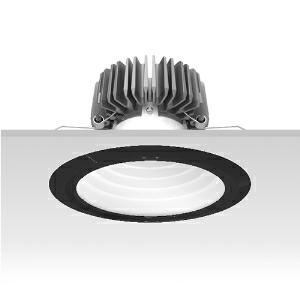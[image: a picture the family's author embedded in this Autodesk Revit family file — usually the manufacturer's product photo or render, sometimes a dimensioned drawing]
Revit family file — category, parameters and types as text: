
# Revit family: 3f_filippi_-_3f_reno_bianco_ampio_3f_filippi_-_30650_a01026_-_3f_reno_200_wh_2000-930_ep_wide___vt_bk_8b70
name_source: partatom
category: Lighting Fixtures
units: mm (PartAtom-declared; Revit-internal decimal feet)

## family parameters
Cut with Voids When Loaded = No
Host = Face
Light Source = No
Part Type = Normal
Room Calculation Point = No
Round Connector Dimension = Use Diameter
Shared = No

## types (1)
- 3F Filippi - 3F Reno Bianco Ampio (1 x LED, 1804 lm, 25 W, 3000 K)
    Apparent Load = 25 VA
    Approval mark = ENEC
    CIE Flux Codes = 75 94 99 100 100
    Color Rendering = 90
    Color Temperature = 3000 K
    Control Gear = Electronic ballast
    Default Elevation = 1800 mm
    Description = ILLUMINOTECHNICAL
Luminous efficiency 100% (DLOR 100%, ULOR 0%).
Initial luminous flux of the luminaire 1804 lm.
Emergency luminaire luminous flux BLF 16.7%.
Direct symmetric wide distribution.
Installation Interdistance Transv.D = 1.56 x hu - Long.D = 1.56 x hu.
Average luminance <3000 cd/m² for radial angles >65°.
Tabular UGR (CIE 117 - 4H-8H; S=0.25H; 70/50/20): RUG 20.6 - 20.5.
Beam angle: 74° - 74°.
Luminous efficacy 72 lm/W.
Lifetime (L90/B10): 30000 h. (tq+25°C)
Lifetime (L85/B10): 50000 h. (tq+25°C)
Lifetime (L70/B10): 80000 h. (tq+25°C)
Sudden decreased luminous flux after 50000 hours: 0% (C0).
Photobiological safety in compliance with IEC/TR 62778: RG0 risk exempt, (IEC 62471).
In compliance with IEC/EN 62722-2-1 - IEC/EN 62717 standards.

SOURCE
Compact LED module 2000/930.
Energy efficiency class (UE 2019/2020 - UE 2019/2015): E.
CIE 13.3 Colour rendering index: CRI >90 (R9 >50%).
IES TM-30 Fidelity Index: Rf = 92 Rg = 101.
CCT nominal colour temperature 3000 K.
Colour initial tolerance (MacAdam): SDCM 3.
Zhaga Book 3 compliant.

MECHANICAL
Passive heat dissipator in die-casting aluminium, oversized, for optimum thermal management of the LED module.
Parabolic element with graduated/concentric rings in white polycarbonate.
Transparent external lens with glossy and satin differentiated surfaces, with a cooling and anti-insect system in methacrylate (PMMA).
Fastening spring clips in stainless steel.
Dimensions: diameter 226 mm, height 146 mm. Weight 1.615 kg.
IP44 protection degree for exposed part, IP20 for recessed part.
Mechanical strength to impacts IK06 (1 joule).
Glow-wire test resistance 650°C.

ELECTRICAL
Wiring on a separate unit.
Halogen Free electronic wiring 230V-50/60Hz, power factor 0.90, THD <25%, constant output current, SELV, class II, 1 driver.
Power of the luminaire 25 W.
CE - IEC 60598-1 - EN 60598-1.
EP maintained emergency wiring on board, 1h duration, 24h recharge; compliant with EN 60598-2-22, excluding high risk areas.
SAFE FLICKER: PstLM=<1 and SVM=<0.4 (IEC TR 61547-1 and IEC TR 63158), to ensure a more comfortable and safe light.
Ambient temperature from +5°C to +25°C.
Temperature class T6 max 85°C.
Relative humidity UR: <85%.

INSTALLATION
Pull-up recessed fitting.
False ceiling carving: 200 mm.
All accessories dedicated to this product are available on the Catalog and on our website www.3F-Filippi.com.

ACCESSORIES
A01026 - VT transparent glass, tempered, not flammable, locked and in line with the trim, in black polycarbonate.

APPLICATIONS
Environments: architectural, commercial, exhibition areas, transit areas, corridors, shops, display windows, service areas.
In false ceilings with narrow voids.

WARNING
Luminaire designed for disposal/recycling at end-of-life.
Replaceable (LED only) light source by a professional. Replaceable control gear by a professional.
    Height = 0 mm  [stored 0 ft]
    Lamp = 1 x LED
    Lamp Light Flux = 1804 lm
    Lamp Power = 25 W
    Lamp count = 1
    Length = 226 mm
    Lifetime = 50000 h
    Luminous efficacy = 72 lm/W
    Manufacturer = 3F Filippi
    ModVariant = No
    Model = 3F Filippi - 30650+A01026 - 3F Reno 200 WH 2000-930 EP WIDE + VT BK
    Mounting Place = Ceiling
    Mounting Type = Recessed
    Number of Poles = 1
    OnlyDefault = Yes
    Power Factor = 1
    Product Name = 3F Filippi - 3F Reno Bianco Ampio
    Product group = recessed luminaire
    ProductGroupID = 4
    Protection Class = Protection class II
    Protection Degree = IP 20
    RLX_Detail_Level = 1
    RLX_Emergency_Light_Flux = 0 lm
    RLX_Emergency_Type = 0
    RLX_Emergency_Type_DB = No
    RlxData = <blob elided: 99565 chars, md5=9da305a2>
    Socket = socket
    Standby Power = 0 W
    System Light Flux = 1804 lm
    System Power = 25 W
    Type Comments = Product without accessories
    Type Image = 3ffilippi_3f_reno_200_wh__a01026.jpg
    URL = http://relux.com
    VarID = ---
    Voltage = 0 V
    Weight = 0.00 kg
    Width = 0 mm  [stored 0 ft]

note: [stored X ft] marks values corroborated as IEEE doubles in the binary element streams (Revit-internal decimal feet)

## geometry (parser evidence)
native form markers: Blend x4, Sweep x11
no freeform markers — native parametric forms only
